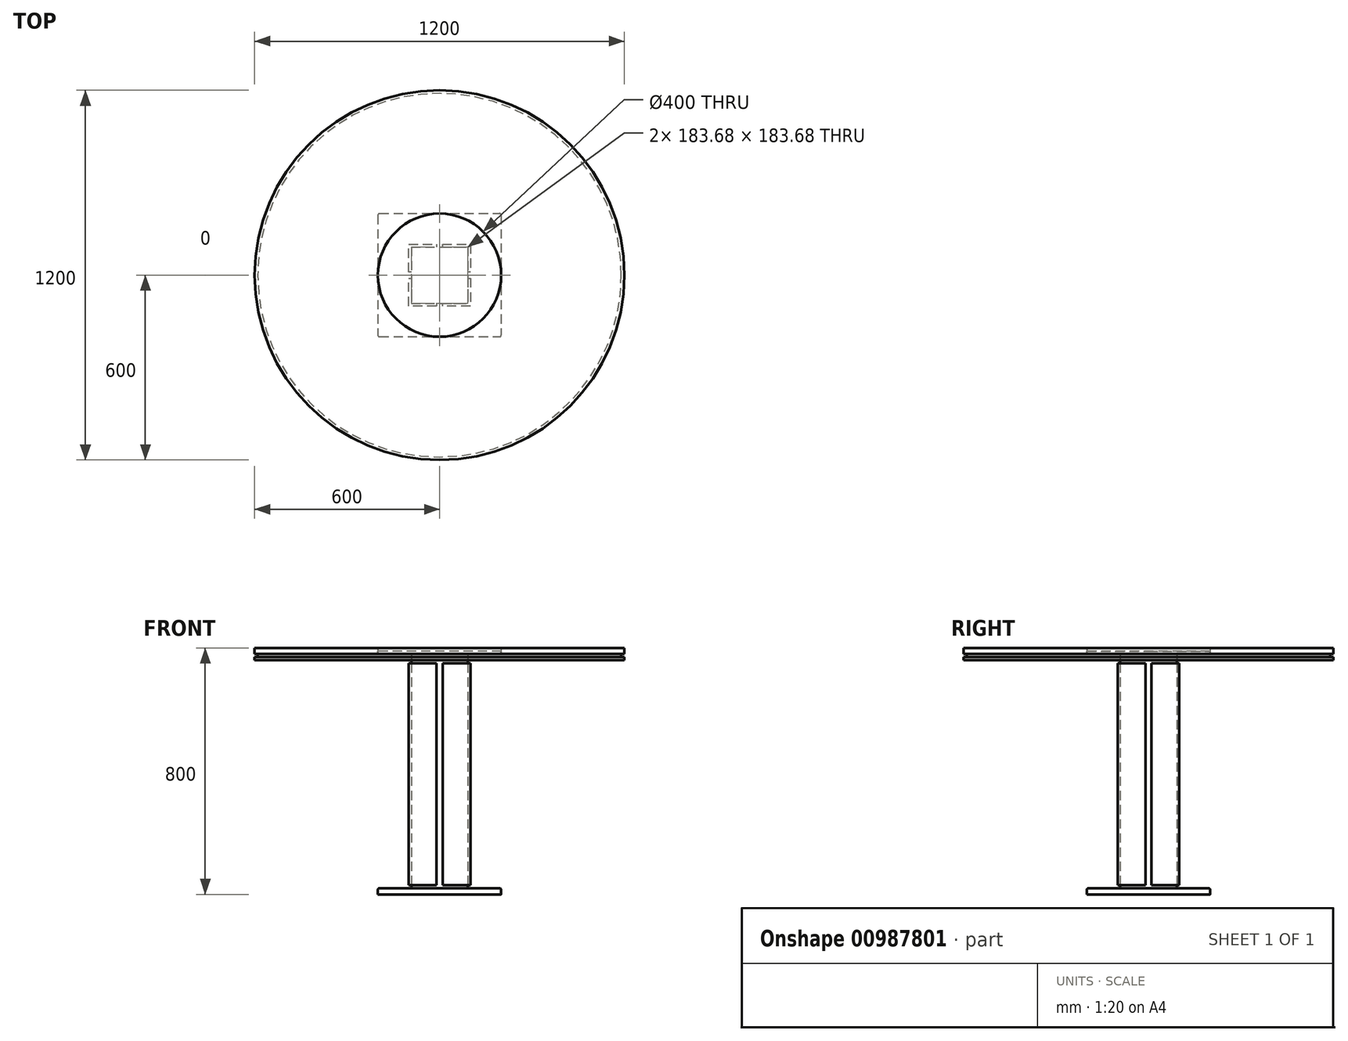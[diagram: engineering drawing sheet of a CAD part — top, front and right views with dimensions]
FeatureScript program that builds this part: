
annotation { "Feature Type Name" : "Feature", "Feature Type Description" : "" }
export const myFeature = defineFeature(function(context is Context, id is Id, definition is map)
    precondition{}
    {
        {
            var Q0;
            Q0=qCreatedBy(makeId("Top.planeOp"),FACE);
            var sketch = newSketch(context, id + "F0", { "sketchPlane" : qUnion([Q0])});
            skLineSegment(sketch, "E0", {"start": v(0, 0) * mm, "end": v(0, 83.68) * mm, "construction": true});
            skLineSegment(sketch, "E1", {"start": v(0, 0) * mm, "end": v(83.68, 0) * mm, "construction": true});
            skPoint(sketch, "E1.endSnap0", {"position": v(83.68, 0) * mm});
            skLineSegment(sketch, "E2.bottom", {"start": v(-200, 200) * mm, "end": v(200, 200) * mm});
            skLineSegment(sketch, "E2.top", {"start": v(-200, -200) * mm, "end": v(200, -200) * mm});
            skLineSegment(sketch, "E2.left", {"start": v(-200, 200) * mm, "end": v(-200, -200) * mm});
            skLineSegment(sketch, "E2.right", {"start": v(200, 200) * mm, "end": v(200, -200) * mm});
            skLineSegment(sketch, "E3", {"start": v(83.68, 0) * mm, "end": v(200, 0) * mm, "construction": true});
            skLineSegment(sketch, "E4", {"start": v(0, 83.68) * mm, "end": v(0, 200) * mm, "construction": true});
            skLineSegment(sketch, "E5", {"start": v(-10, 83.68) * mm, "end": v(10, 83.68) * mm});
            skLineSegment(sketch, "E6", {"start": v(10, 83.68) * mm, "end": v(10, 100) * mm});
            skLineSegment(sketch, "E7", {"start": v(10, 100) * mm, "end": v(100, 100) * mm});
            skLineSegment(sketch, "E8", {"start": v(100, 100) * mm, "end": v(100, 10) * mm});
            skLineSegment(sketch, "E9", {"start": v(100, 10) * mm, "end": v(83.68, 10) * mm});
            skLineSegment(sketch, "E10", {"start": v(83.68, 10) * mm, "end": v(83.68, -10) * mm});
            skLineSegment(sketch, "E11", {"start": v(83.68, -10) * mm, "end": v(100, -10) * mm});
            skLineSegment(sketch, "E12", {"start": v(100, -10) * mm, "end": v(100, -100) * mm});
            skLineSegment(sketch, "E13", {"start": v(100, -100) * mm, "end": v(10, -100) * mm});
            skLineSegment(sketch, "E14", {"start": v(10, -100) * mm, "end": v(10, -83.68) * mm});
            skLineSegment(sketch, "E15", {"start": v(10, -83.68) * mm, "end": v(-10, -83.68) * mm});
            skLineSegment(sketch, "E16", {"start": v(-10, -83.68) * mm, "end": v(-10, -100) * mm});
            skLineSegment(sketch, "E17", {"start": v(-10, -100) * mm, "end": v(-100, -100) * mm});
            skLineSegment(sketch, "E18", {"start": v(-100, -100) * mm, "end": v(-100, -10) * mm});
            skLineSegment(sketch, "E19", {"start": v(-100, -10) * mm, "end": v(-83.68, -10) * mm});
            skLineSegment(sketch, "E20", {"start": v(-83.68, -10) * mm, "end": v(-83.68, 10) * mm});
            skLineSegment(sketch, "E21", {"start": v(-83.68, 10) * mm, "end": v(-100, 10) * mm});
            skLineSegment(sketch, "E22", {"start": v(-100, 10) * mm, "end": v(-100, 100) * mm});
            skLineSegment(sketch, "E23", {"start": v(-100, 100) * mm, "end": v(-10, 100) * mm});
            skLineSegment(sketch, "E24", {"start": v(-10, 100) * mm, "end": v(-10, 83.68) * mm});
            skLineSegment(sketch, "E25", {"start": v(-10, 91.84) * mm, "end": v(10, 91.84) * mm});
            skLineSegment(sketch, "E26", {"start": v(-91.84, 10) * mm, "end": v(-91.84, -10) * mm});
            skLineSegment(sketch, "E27", {"start": v(-10, -91.84) * mm, "end": v(10, -91.84) * mm});
            skLineSegment(sketch, "E28", {"start": v(91.84, 10) * mm, "end": v(91.84, -10) * mm});
            skLineSegment(sketch, "E29.bottom", {"start": v(-91.84, 91.84) * mm, "end": v(91.84, 91.84) * mm});
            skLineSegment(sketch, "E29.top", {"start": v(-91.84, -91.84) * mm, "end": v(91.84, -91.84) * mm});
            skLineSegment(sketch, "E29.left", {"start": v(-91.84, 91.84) * mm, "end": v(-91.84, -91.84) * mm});
            skLineSegment(sketch, "E29.right", {"start": v(91.84, 91.84) * mm, "end": v(91.84, -91.84) * mm});
            skSolve(sketch);
        }
        {
            var Q0;
            {var subQ18=sQuery(id+"F0.wireOp",EDGE,"E5");Q0=makeQuery(id+"F0.imprint","IMPRINT",FACE,{"disambiguationData":[TD([[makeQuery(id+"F0.imprint","IMPRINT",EDGE,{"derivedFrom":subQ18}),-1.0]])]});}
            var Q1;
            {var subQ4=sQuery(id+"F0.wireOp",EDGE,"E22");Q1=makeQuery(id+"F0.imprint","IMPRINT",FACE,{"disambiguationData":[TD([[makeQuery(id+"F0.imprint","IMPRINT",EDGE,{"derivedFrom":subQ4}),-1.0]])]});}
            var Q2;
            {var subQ4=sQuery(id+"F0.wireOp",EDGE,"E17");Q2=makeQuery(id+"F0.imprint","IMPRINT",FACE,{"disambiguationData":[TD([[makeQuery(id+"F0.imprint","IMPRINT",EDGE,{"derivedFrom":subQ4}),-1.0]])]});}
            var Q3;
            {var subQ6=sQuery(id+"F0.wireOp",EDGE,"E12");Q3=makeQuery(id+"F0.imprint","IMPRINT",FACE,{"disambiguationData":[TD([[makeQuery(id+"F0.imprint","IMPRINT",EDGE,{"derivedFrom":subQ6}),-1.0]])]});}
            var Q4;
            {var subQ6=sQuery(id+"F0.wireOp",EDGE,"E7");Q4=makeQuery(id+"F0.imprint","IMPRINT",FACE,{"disambiguationData":[TD([[makeQuery(id+"F0.imprint","IMPRINT",EDGE,{"derivedFrom":subQ6}),-1.0]])]});}
            extrude(context, id + "F1", {"entities" : qUnion([Q0, Q1, Q2, Q3, Q4]), "depth" : 750 * mm, "offsetDistance" : 25 * mm, "hasSecondDirection" : true, "secondDirectionOppositeDirection" : false, "secondDirectionDepth" : 30 * mm});
        }
        {
            var Q0;
            {var subQ0=sQuery(id+"F0.wireOp",EDGE,"E15");Q0=makeQuery(id+"F0.imprint","IMPRINT",FACE,{"disambiguationData":[TD([[makeQuery(id+"F0.imprint","IMPRINT",EDGE,{"derivedFrom":subQ0}),1.0]])]});}
            var Q1;
            {var subQ0=sQuery(id+"F0.wireOp",EDGE,"E10");Q1=makeQuery(id+"F0.imprint","IMPRINT",FACE,{"disambiguationData":[TD([[makeQuery(id+"F0.imprint","IMPRINT",EDGE,{"derivedFrom":subQ0}),1.0]])]});}
            var Q2;
            {var subQ0=sQuery(id+"F0.wireOp",EDGE,"E5");Q2=makeQuery(id+"F0.imprint","IMPRINT",FACE,{"disambiguationData":[TD([[makeQuery(id+"F0.imprint","IMPRINT",EDGE,{"derivedFrom":subQ0}),1.0]])]});}
            var Q3;
            {var subQ0=sQuery(id+"F0.wireOp",EDGE,"E20");Q3=makeQuery(id+"F0.imprint","IMPRINT",FACE,{"disambiguationData":[TD([[makeQuery(id+"F0.imprint","IMPRINT",EDGE,{"derivedFrom":subQ0}),1.0]])]});}
            extrude(context, id + "F2", {"entities" : qUnion([Q0, Q1, Q2, Q3]), "depth" : 750 * mm, "offsetDistance" : 25 * mm, "hasSecondDirection" : true, "secondDirectionOppositeDirection" : false, "secondDirectionDepth" : 30 * mm});
        }
        {
            var Q0;
            {var subQ19=sQuery(id+"F0.wireOp",EDGE,"E5");Q0=makeQuery(id+"F0.imprint","IMPRINT",FACE,{"disambiguationData":[TD([[makeQuery(id+"F0.imprint","IMPRINT",EDGE,{"derivedFrom":subQ19}),-1.0]])]});}
            var Q1;
            {var subQ0=sQuery(id+"F0.wireOp",EDGE,"E15");Q1=makeQuery(id+"F0.imprint","IMPRINT",FACE,{"disambiguationData":[TD([[makeQuery(id+"F0.imprint","IMPRINT",EDGE,{"derivedFrom":subQ0}),1.0]])]});}
            var Q2;
            {var subQ0=sQuery(id+"F0.wireOp",EDGE,"E10");Q2=makeQuery(id+"F0.imprint","IMPRINT",FACE,{"disambiguationData":[TD([[makeQuery(id+"F0.imprint","IMPRINT",EDGE,{"derivedFrom":subQ0}),1.0]])]});}
            var Q3;
            {var subQ0=sQuery(id+"F0.wireOp",EDGE,"E5");Q3=makeQuery(id+"F0.imprint","IMPRINT",FACE,{"disambiguationData":[TD([[makeQuery(id+"F0.imprint","IMPRINT",EDGE,{"derivedFrom":subQ0}),1.0]])]});}
            var Q4;
            {var subQ0=sQuery(id+"F0.wireOp",EDGE,"E20");Q4=makeQuery(id+"F0.imprint","IMPRINT",FACE,{"disambiguationData":[TD([[makeQuery(id+"F0.imprint","IMPRINT",EDGE,{"derivedFrom":subQ0}),1.0]])]});}
            extrude(context, id + "F3", {"entities" : qUnion([Q0, Q1, Q2, Q3, Q4]), "operationType" : NewBodyOperationType.ADD, "depth" : 30 * mm, "offsetDistance" : 25 * mm, "hasSecondDirection" : true, "secondDirectionOppositeDirection" : false, "secondDirectionDepth" : 20 * mm});
        }
        {
            var Q0;
            {var subQ19=sQuery(id+"F0.wireOp",EDGE,"E5");Q0=makeQuery(id+"F0.imprint","IMPRINT",FACE,{"disambiguationData":[TD([[makeQuery(id+"F0.imprint","IMPRINT",EDGE,{"derivedFrom":subQ19}),-1.0]])]});}
            var Q1;
            {var subQ0=sQuery(id+"F0.wireOp",EDGE,"E5");Q1=makeQuery(id+"F0.imprint","IMPRINT",FACE,{"disambiguationData":[TD([[makeQuery(id+"F0.imprint","IMPRINT",EDGE,{"derivedFrom":subQ0}),1.0]])]});}
            var Q2;
            {var subQ0=sQuery(id+"F0.wireOp",EDGE,"E20");Q2=makeQuery(id+"F0.imprint","IMPRINT",FACE,{"disambiguationData":[TD([[makeQuery(id+"F0.imprint","IMPRINT",EDGE,{"derivedFrom":subQ0}),1.0]])]});}
            var Q3;
            {var subQ0=sQuery(id+"F0.wireOp",EDGE,"E15");Q3=makeQuery(id+"F0.imprint","IMPRINT",FACE,{"disambiguationData":[TD([[makeQuery(id+"F0.imprint","IMPRINT",EDGE,{"derivedFrom":subQ0}),1.0]])]});}
            var Q4;
            {var subQ0=sQuery(id+"F0.wireOp",EDGE,"E10");Q4=makeQuery(id+"F0.imprint","IMPRINT",FACE,{"disambiguationData":[TD([[makeQuery(id+"F0.imprint","IMPRINT",EDGE,{"derivedFrom":subQ0}),1.0]])]});}
            extrude(context, id + "F4", {"entities" : qUnion([Q0, Q1, Q2, Q3, Q4]), "operationType" : NewBodyOperationType.ADD, "depth" : 760 * mm, "offsetDistance" : 25 * mm, "hasSecondDirection" : true, "secondDirectionOppositeDirection" : false, "secondDirectionDepth" : 750 * mm});
        }
        {
            var Q0;
            Q0=makeQuery(id+"F0.imprint","IMPRINT",FACE,{"disambiguationData":[TD([[makeQuery(id+"F0.imprint","IMPRINT",EDGE,{"derivedFrom":sQuery(id+"F0.wireOp",EDGE,"E2.bottom")}),-1.0]])]});
            var Q1;
            {var subQ4=sQuery(id+"F0.wireOp",EDGE,"E22");Q1=makeQuery(id+"F0.imprint","IMPRINT",FACE,{"disambiguationData":[TD([[makeQuery(id+"F0.imprint","IMPRINT",EDGE,{"derivedFrom":subQ4}),-1.0]])]});}
            var Q2;
            {var subQ6=sQuery(id+"F0.wireOp",EDGE,"E7");Q2=makeQuery(id+"F0.imprint","IMPRINT",FACE,{"disambiguationData":[TD([[makeQuery(id+"F0.imprint","IMPRINT",EDGE,{"derivedFrom":subQ6}),-1.0]])]});}
            var Q3;
            {var subQ6=sQuery(id+"F0.wireOp",EDGE,"E12");Q3=makeQuery(id+"F0.imprint","IMPRINT",FACE,{"disambiguationData":[TD([[makeQuery(id+"F0.imprint","IMPRINT",EDGE,{"derivedFrom":subQ6}),-1.0]])]});}
            var Q4;
            {var subQ4=sQuery(id+"F0.wireOp",EDGE,"E17");Q4=makeQuery(id+"F0.imprint","IMPRINT",FACE,{"disambiguationData":[TD([[makeQuery(id+"F0.imprint","IMPRINT",EDGE,{"derivedFrom":subQ4}),-1.0]])]});}
            var Q5;
            {var subQ0=sQuery(id+"F0.wireOp",EDGE,"E20");Q5=makeQuery(id+"F0.imprint","IMPRINT",FACE,{"disambiguationData":[TD([[makeQuery(id+"F0.imprint","IMPRINT",EDGE,{"derivedFrom":subQ0}),1.0]])]});}
            var Q6;
            {var subQ0=sQuery(id+"F0.wireOp",EDGE,"E5");Q6=makeQuery(id+"F0.imprint","IMPRINT",FACE,{"disambiguationData":[TD([[makeQuery(id+"F0.imprint","IMPRINT",EDGE,{"derivedFrom":subQ0}),1.0]])]});}
            var Q7;
            {var subQ0=sQuery(id+"F0.wireOp",EDGE,"E10");Q7=makeQuery(id+"F0.imprint","IMPRINT",FACE,{"disambiguationData":[TD([[makeQuery(id+"F0.imprint","IMPRINT",EDGE,{"derivedFrom":subQ0}),1.0]])]});}
            var Q8;
            {var subQ0=sQuery(id+"F0.wireOp",EDGE,"E15");Q8=makeQuery(id+"F0.imprint","IMPRINT",FACE,{"disambiguationData":[TD([[makeQuery(id+"F0.imprint","IMPRINT",EDGE,{"derivedFrom":subQ0}),1.0]])]});}
            var Q9;
            {var subQ19=sQuery(id+"F0.wireOp",EDGE,"E5");Q9=makeQuery(id+"F0.imprint","IMPRINT",FACE,{"disambiguationData":[TD([[makeQuery(id+"F0.imprint","IMPRINT",EDGE,{"derivedFrom":subQ19}),-1.0]])]});}
            extrude(context, id + "F5", {"entities" : qUnion([Q0, Q1, Q2, Q3, Q4, Q5, Q6, Q7, Q8, Q9]), "operationType" : NewBodyOperationType.ADD, "depth" : 20 * mm, "offsetDistance" : 25 * mm});
        }
        {
            var Q0;
            Q0=makeQuery(id+"F4.opExtrude","CAP_FACE",FACE,{"disambiguationData":[OSD([sQuery(id+"F0.wireOp",EDGE,"E29.bottom"),sQuery(id+"F0.wireOp",EDGE,"E29.top"),sQuery(id+"F0.wireOp",EDGE,"E29.left"),sQuery(id+"F0.wireOp",EDGE,"E29.right")])],"isStart":false});
            var sketch = newSketch(context, id + "F6", { "sketchPlane" : qUnion([Q0])});
            skCircle(sketch, "E30", {"center": v(0, 0) * mm, "radius": 200 * mm});
            skCircle(sketch, "E31", {"center": v(0, 0) * mm, "radius": 590 * mm});
            skCircle(sketch, "E32", {"center": v(0, 0) * mm, "radius": 600 * mm});
            skSolve(sketch);
        }
        {
            var Q0;
            Q0=makeQuery(id+"F6.imprint","IMPRINT",FACE,{"disambiguationData":[TD([[makeQuery(id+"F6.imprint","IMPRINT",EDGE,{"derivedFrom":sQuery(id+"F6.wireOp",EDGE,"E30")}),-1.0]])]});
            var Q1;
            Q1=makeQuery(id+"F6.imprint","IMPRINT",FACE,{"disambiguationData":[TD([[makeQuery(id+"F6.imprint","IMPRINT",EDGE,{"derivedFrom":sQuery(id+"F6.wireOp",EDGE,"E31")}),-1.0]])]});
            extrude(context, id + "F7", {"entities" : qUnion([Q0, Q1]), "depth" : 40 * mm, "offsetDistance" : 25 * mm, "hasSecondDirection" : true, "secondDirectionOppositeDirection" : false, "secondDirectionDepth" : 20 * mm});
        }
        {
            var Q0;
            Q0=makeQuery(id+"F6.imprint","IMPRINT",FACE,{"disambiguationData":[TD([[makeQuery(id+"F6.imprint","IMPRINT",EDGE,{"derivedFrom":sQuery(id+"F6.wireOp",EDGE,"E30")}),1.0]])]});
            var Q1;
            Q1=makeQuery(id+"F6.imprint","IMPRINT",FACE,{"disambiguationData":[TD([[makeQuery(id+"F6.imprint","IMPRINT",EDGE,{"derivedFrom":sQuery(id+"F6.wireOp",EDGE,"E30")}),-1.0]])]});
            extrude(context, id + "F8", {"entities" : qUnion([Q0, Q1]), "depth" : 20 * mm, "offsetDistance" : 25 * mm, "hasSecondDirection" : true, "secondDirectionOppositeDirection" : false, "secondDirectionDepth" : 10 * mm});
        }
        {
            var Q0;
            Q0=makeQuery(id+"F6.imprint","IMPRINT",FACE,{"disambiguationData":[TD([[makeQuery(id+"F6.imprint","IMPRINT",EDGE,{"derivedFrom":sQuery(id+"F6.wireOp",EDGE,"E30")}),-1.0]])]});
            var Q1;
            Q1=makeQuery(id+"F6.imprint","IMPRINT",FACE,{"disambiguationData":[TD([[makeQuery(id+"F6.imprint","IMPRINT",EDGE,{"derivedFrom":sQuery(id+"F6.wireOp",EDGE,"E30")}),1.0]])]});
            var Q2;
            Q2=makeQuery(id+"F6.imprint","IMPRINT",FACE,{"disambiguationData":[TD([[makeQuery(id+"F6.imprint","IMPRINT",EDGE,{"derivedFrom":sQuery(id+"F6.wireOp",EDGE,"E31")}),-1.0]])]});
            extrude(context, id + "F9", {"entities" : qUnion([Q0, Q1, Q2]), "depth" : 10 * mm, "offsetDistance" : 25 * mm});
        }
        {
            var Q0;
            Q0=makeQuery(id+"F6.imprint","IMPRINT",FACE,{"disambiguationData":[TD([[makeQuery(id+"F6.imprint","IMPRINT",EDGE,{"derivedFrom":makeQuery(id+"F4.opExtrude","CAP_EDGE",EDGE,{"disambiguationData":[OSD([sQuery(id+"F0.wireOp",EDGE,"E29.bottom")])],"isStart":false})}),-1.0]])]});
            var Q1;
            Q1=makeQuery(id+"F6.imprint","IMPRINT",FACE,{"disambiguationData":[TD([[makeQuery(id+"F6.imprint","IMPRINT",EDGE,{"derivedFrom":sQuery(id+"F6.wireOp",EDGE,"E30")}),1.0]])]});
            extrude(context, id + "F10", {"entities" : qUnion([Q0, Q1]), "depth" : 40 * mm, "offsetDistance" : 25 * mm, "hasSecondDirection" : true, "secondDirectionOppositeDirection" : false, "secondDirectionDepth" : 30 * mm});
        }
        {
            var Q0;
            Q0=makeQuery(id+"F10.opExtrude","CAP_FACE",FACE,{"disambiguationData":[OSD([sQuery(id+"F6.wireOp",EDGE,"E30")])],"isStart":true});
            extrude(context, id + "F11", {"entities" : qUnion([Q0]), "depth" : 10 * mm, "offsetDistance" : 25 * mm});
        }
        {
            var Q0;
            Q0=makeQuery(id+"F5.opExtrude","CAP_EDGE",EDGE,{"disambiguationData":[OSD([sQuery(id+"F0.wireOp",EDGE,"E2.top")])],"isStart":false});
            var Q1;
            Q1=makeQuery(id+"F5.opExtrude","CAP_EDGE",EDGE,{"disambiguationData":[OSD([sQuery(id+"F0.wireOp",EDGE,"E2.left")])],"isStart":false});
            var Q2;
            Q2=makeQuery(id+"F5.opExtrude","CAP_EDGE",EDGE,{"disambiguationData":[OSD([sQuery(id+"F0.wireOp",EDGE,"E2.bottom")])],"isStart":false});
            var Q3;
            Q3=makeQuery(id+"F5.opExtrude","CAP_EDGE",EDGE,{"disambiguationData":[OSD([sQuery(id+"F0.wireOp",EDGE,"E2.right")])],"isStart":false});
            var Q4;
            Q4=makeQuery(id+"F5.opExtrude","SWEPT_EDGE",EDGE,{"disambiguationData":[OSD([sQuery(id+"F0.wireOp",EDGE,"E2.bottom"),sQuery(id+"F0.wireOp",EDGE,"E2.right")])]});
            var Q5;
            Q5=makeQuery(id+"F5.opExtrude","SWEPT_EDGE",EDGE,{"disambiguationData":[OSD([sQuery(id+"F0.wireOp",EDGE,"E2.bottom"),sQuery(id+"F0.wireOp",EDGE,"E2.left")])]});
            var Q6;
            Q6=makeQuery(id+"F5.opExtrude","SWEPT_EDGE",EDGE,{"disambiguationData":[OSD([sQuery(id+"F0.wireOp",EDGE,"E2.top"),sQuery(id+"F0.wireOp",EDGE,"E2.left")])]});
            var Q7;
            Q7=makeQuery(id+"F5.opExtrude","SWEPT_EDGE",EDGE,{"disambiguationData":[OSD([sQuery(id+"F0.wireOp",EDGE,"E2.top"),sQuery(id+"F0.wireOp",EDGE,"E2.right")])]});
            fillet(context, id + "F12", {"entities" : qUnion([Q0, Q1, Q2, Q3, Q4, Q5, Q6, Q7]), "radius" : 5 * mm, "tangentPropagation" : true, "allowEdgeOverflow" : false});
        }
    });
